# Revit family: Franke_Refrigeration_side_unit_SU12_CM-A1000_FM_CM(EU,CH,GB)
name_source: partatom
category: Specialty Equipment
revit_build: Autodesk Revit 2015 (Build: 20140606_1530(x64)
units: mm (PartAtom-declared; Revit-internal decimal feet)

## types (2) — shared parameters
Assembly Code = Refrigeration side unit SU12
Current consumption = 0.72 A
Cycle = 50 Hz
Cycle Alternative = 60 Hz
Depth (mm) = 475 mm  [stored 1.5584 ft]
Description = Refrigeration side unit SU12 for storage of cooled milk
Energy loss acc. to DIN 18873 = 0.783 kWh/24 h - 230 V
Height (mm) = 586 mm  [stored 1.92257 ft]
Keynote = Refrigeration side unit SU12
Manufacturer = Franke
Max Overcurrent Protection = -
Milk storage = 12 l
Model = 410874 - Refrigeration side unit SU12 CM - A1000 FM CM
Number of Nutral Conductors = 1
Number of Poles = 1
Number of Protective Conductors = 1
Temperature range = + 3° C to +8° C
URL = https://www.franke.com
Volts max. = 240 V
Volts min. = 220 V
Weight = 26 kg
Width (mm) = 340 mm  [stored 1.11549 ft]
zero-valued in all types: Cost

## type names (no varying parameters)
- Refrigeration side unit SU12 CM-A1000 FM CM(220-240V/black line/EU,CH,GB)
- Refrigeration side unit SU12 CM-A1000 FM CM(220-240V/anthracite/EU,CH,GB)

note: [stored X ft] marks values corroborated as IEEE doubles in the binary element streams (Revit-internal decimal feet)
